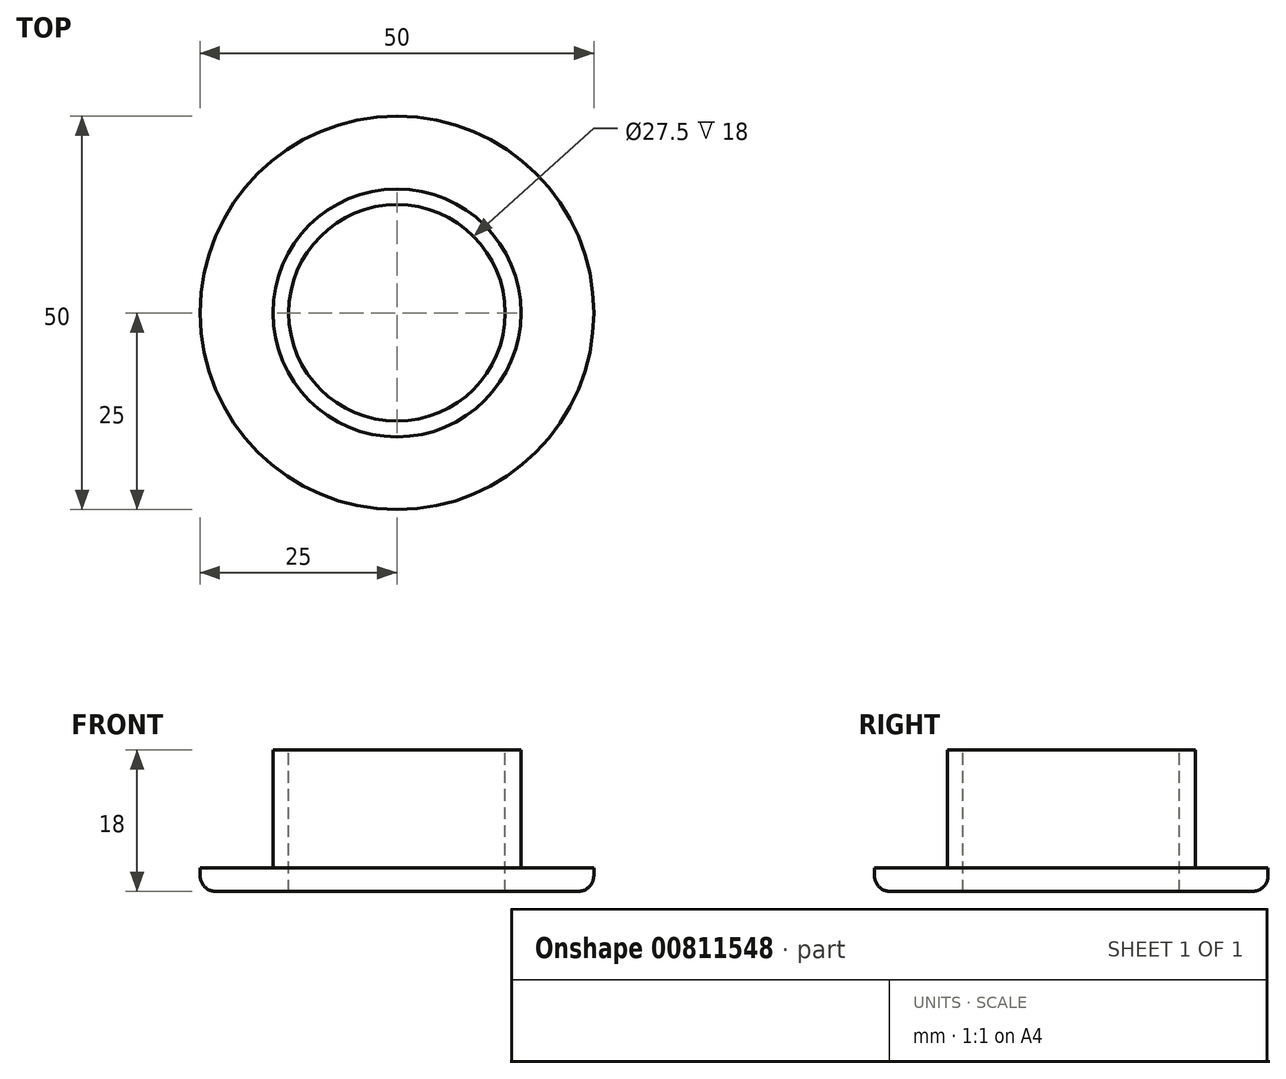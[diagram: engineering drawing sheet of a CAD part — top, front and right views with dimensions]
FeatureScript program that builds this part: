
annotation { "Feature Type Name" : "Feature", "Feature Type Description" : "" }
export const myFeature = defineFeature(function(context is Context, id is Id, definition is map)
    precondition{}
    {
        {
            var Q0;
            Q0=qCreatedBy(makeId("Top.planeOp"),FACE);
            var sketch = newSketch(context, id + "F0", { "sketchPlane" : qUnion([Q0])});
            skCircle(sketch, "E0", {"center": v(0, 0) * mm, "radius": 25 * mm});
            skSolve(sketch);
        }
        {
            var Q0;
            Q0=makeQuery(id+"F0.imprint","IMPRINT",FACE,{"disambiguationData":[TD([[makeQuery(id+"F0.imprint","IMPRINT",EDGE,{"derivedFrom":sQuery(id+"F0.wireOp",EDGE,"E0")}),1.0]])]});
            extrude(context, id + "F1", {"entities" : qUnion([Q0]), "depth" : 3 * mm, "offsetDistance" : 25 * mm});
        }
        {
            var Q0;
            Q0=makeQuery(id+"F1.opExtrude","CAP_FACE",FACE,{"disambiguationData":[OSD([sQuery(id+"F0.wireOp",EDGE,"E0")])],"isStart":false});
            var sketch = newSketch(context, id + "F2", { "sketchPlane" : qUnion([Q0])});
            skCircle(sketch, "E1", {"center": v(0, 0) * mm, "radius": 15.75 * mm});
            skSolve(sketch);
        }
        {
            var Q0;
            Q0 = qSketchRegion(id + "F2", true);
            extrude(context, id + "F3", {"entities" : qUnion([Q0]), "operationType" : NewBodyOperationType.ADD, "depth" : 15 * mm, "offsetDistance" : 25 * mm});
        }
        {
            var Q0;
            Q0=makeQuery(id+"F3.opExtrude","CAP_FACE",FACE,{"disambiguationData":[OSD([sQuery(id+"F2.wireOp",EDGE,"E1")])],"isStart":false});
            var sketch = newSketch(context, id + "F4", { "sketchPlane" : qUnion([Q0])});
            skCircle(sketch, "E2", {"center": v(0, 0) * mm, "radius": 13.75 * mm});
            skSolve(sketch);
        }
        {
            var Q0;
            Q0 = qSketchRegion(id + "F4", true);
            var Q1;
            Q1=makeQuery(id+"F1.opExtrude","CAP_FACE",FACE,{"disambiguationData":[OSD([sQuery(id+"F0.wireOp",EDGE,"E0")])],"isStart":true});
            extrude(context, id + "F5", {"entities" : qUnion([Q0]), "operationType" : NewBodyOperationType.REMOVE, "endBound" : BoundingType.UP_TO_SURFACE, "oppositeDirection" : true, "depth" : 25 * mm, "endBoundEntityFace" : qUnion([Q1]), "offsetDistance" : 25 * mm});
        }
        {
            var Q0;
            Q0=makeQuery(id+"F1.opExtrude","CAP_EDGE",EDGE,{"disambiguationData":[OSD([sQuery(id+"F0.wireOp",EDGE,"E0")])],"isStart":true});
            var Q1;
            Q1=makeQuery(id+"F5.boolean.opBoolean","COPY",EDGE,{"derivedFrom":makeQuery(id+"F5.opExtrude","CAP_EDGE",EDGE,{"disambiguationData":[OSD([sQuery(id+"F4.wireOp",EDGE,"E2")])],"isStart":false})});
            var Q2;
            Q2=makeQuery(id+"F5.boolean.opBoolean","COPY",EDGE,{"derivedFrom":makeQuery(id+"F5.opExtrude","CAP_EDGE",EDGE,{"disambiguationData":[OSD([sQuery(id+"F4.wireOp",EDGE,"E2")])],"isStart":true})});
            fillet(context, id + "F6", {"entities" : qUnion([Q0, Q1, Q2]), "radius" : 2 * mm, "tangentPropagation" : true, "allowEdgeOverflow" : false});
        }
    });
